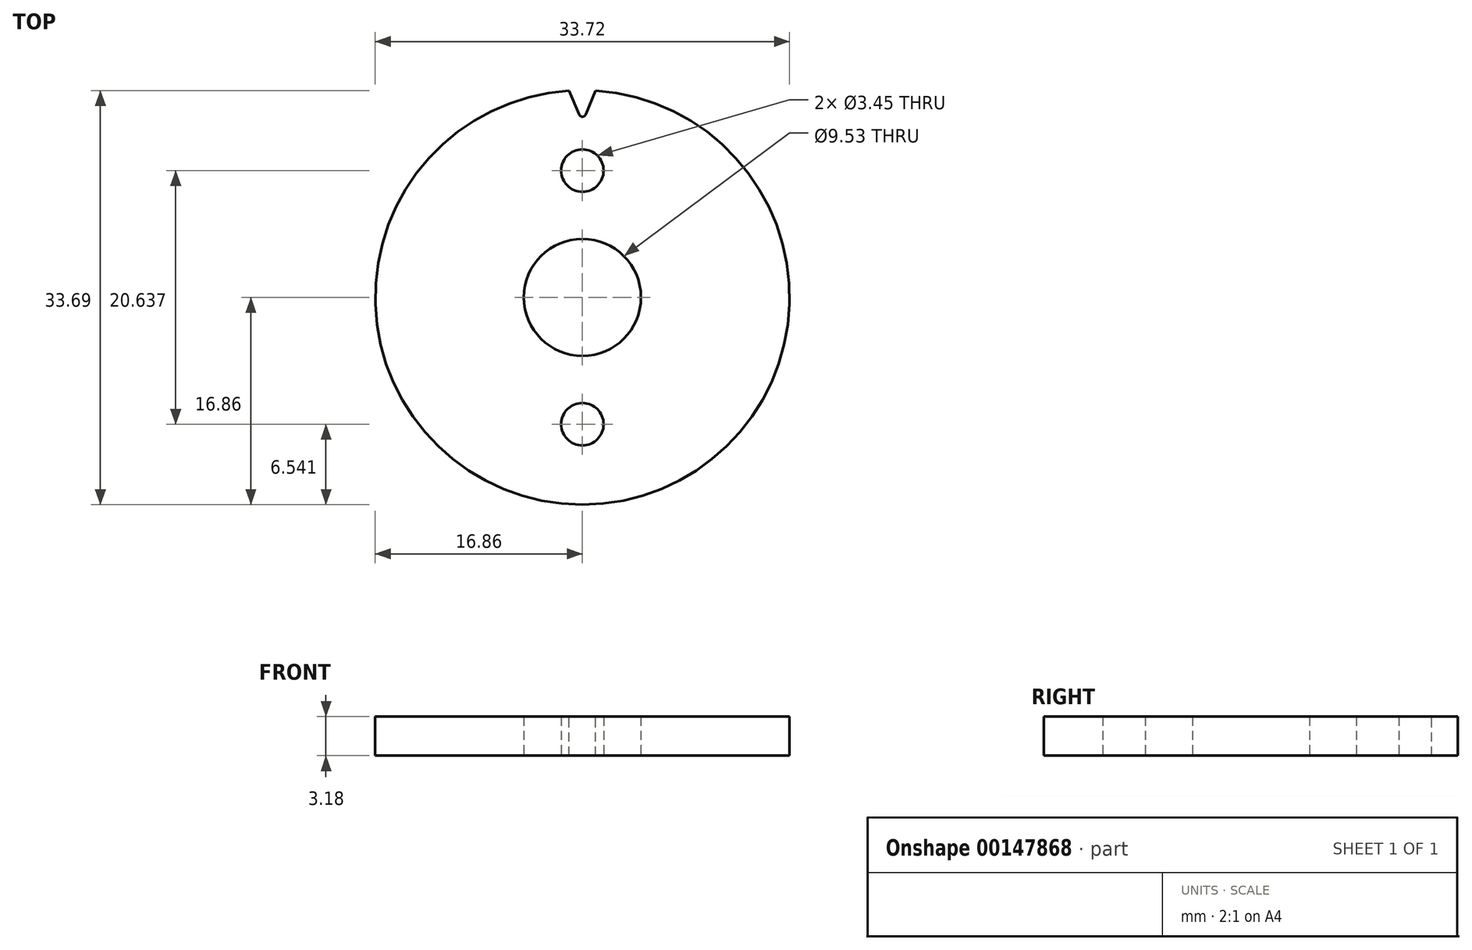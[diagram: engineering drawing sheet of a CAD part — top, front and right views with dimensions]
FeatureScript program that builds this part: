
annotation { "Feature Type Name" : "Feature", "Feature Type Description" : "" }
export const myFeature = defineFeature(function(context is Context, id is Id, definition is map)
    precondition{}
    {
        {
            var Q0;
            Q0=qCreatedBy(makeId("Top.planeOp"),FACE);
            var sketch = newSketch(context, id + "F0", { "sketchPlane" : qUnion([Q0])});
            skCircle(sketch, "E0", {"center": v(0, 0) * mm, "radius": 16.86 * mm});
            skCircle(sketch, "E1", {"center": v(0, -10.32) * mm, "radius": 5.56 * mm, "construction": true});
            skCircle(sketch, "E2", {"center": v(0, -10.32) * mm, "radius": 1.73 * mm});
            skLineSegment(sketch, "E3", {"start": v(0, 10.32) * mm, "end": v(0, -10.32) * mm, "construction": true});
            skCircle(sketch, "E4", {"center": v(0, 10.32) * mm, "radius": 1.73 * mm});
            skCircle(sketch, "E5", {"center": v(0, 0) * mm, "radius": 4.76 * mm});
            skSolve(sketch);
        }
        {
            var Q0;
            Q0=makeQuery(id+"F0.imprint","IMPRINT",FACE,{"disambiguationData":[TD([[makeQuery(id+"F0.imprint","IMPRINT",EDGE,{"derivedFrom":sQuery(id+"F0.wireOp",EDGE,"d7zeTPih-CRss-xDOh-gPdP-rmPCdwzH7cdN.left")}),1.0]])]});
            var Q1;
            Q1=makeQuery(id+"F0.imprint","IMPRINT",FACE,{"disambiguationData":[TD([[makeQuery(id+"F0.imprint","IMPRINT",EDGE,{"derivedFrom":sQuery(id+"F0.wireOp",EDGE,"E0")}),1.0]])]});
            extrude(context, id + "F1", {"entities" : qUnion([Q0, Q1]), "depth" : 3.17 * mm});
        }
        {
            var Q0;
            Q0=makeQuery(id+"F1.opExtrude","CAP_FACE",FACE,{"disambiguationData":[OSD([sQuery(id+"F0.wireOp",EDGE,"d7zeTPih-CRss-xDOh-gPdP-rmPCdwzH7cdN.left"),sQuery(id+"F0.wireOp",EDGE,"d7zeTPih-CRss-xDOh-gPdP-rmPCdwzH7cdN.right"),sQuery(id+"F0.wireOp",EDGE,"ScfBMfkV-s1yN-Ls9R-SGr5-fEyGpD6zak8e"),sQuery(id+"F0.wireOp",EDGE,"xnxmVwjl-FvSF-m7sj-be2U-u85gZZGoORGZ"),sQuery(id+"F0.wireOp",EDGE,"E0")])],"isStart":false});
            var sketch = newSketch(context, id + "F2", { "sketchPlane" : qUnion([Q0])});
            skLineSegment(sketch, "E6", {"start": v(0, 0) * mm, "end": v(0, 16.86) * mm, "construction": true});
            skLineSegment(sketch, "E7", {"start": v(0, 0) * mm, "end": v(0.72, 16.85) * mm, "construction": true});
            skArc(sketch, "E8", {"start": v(1.08, 16.83) * mm, "mid": v(0, 16.86) * mm, "end": v(-1.08, 16.83) * mm});
            skLineSegment(sketch, "E9", {"start": v(-1.08, 16.83) * mm, "end": v(-0.28, 14.88) * mm});
            skLineSegment(sketch, "E10", {"start": v(1.08, 16.83) * mm, "end": v(0.28, 14.88) * mm});
            skPoint(sketch, "E11", {"position": v(0.68, 15.85) * mm});
            skArc(sketch, "E12", {"start": v(-0.28, 14.88) * mm, "mid": v(0, 14.7) * mm, "end": v(0.28, 14.88) * mm});
            skSolve(sketch);
        }
        {
            var Q0;
            Q0=qSketchRegion(id+"F2",true);
            var Q1;
            Q1=makeQuery(id+"F1.opExtrude","CAP_FACE",FACE,{"disambiguationData":[OSD([sQuery(id+"F0.wireOp",EDGE,"d7zeTPih-CRss-xDOh-gPdP-rmPCdwzH7cdN.left"),sQuery(id+"F0.wireOp",EDGE,"d7zeTPih-CRss-xDOh-gPdP-rmPCdwzH7cdN.right"),sQuery(id+"F0.wireOp",EDGE,"ScfBMfkV-s1yN-Ls9R-SGr5-fEyGpD6zak8e"),sQuery(id+"F0.wireOp",EDGE,"xnxmVwjl-FvSF-m7sj-be2U-u85gZZGoORGZ"),sQuery(id+"F0.wireOp",EDGE,"E0")])],"isStart":true});
            extrude(context, id + "F3", {"entities" : qUnion([Q0]), "operationType" : NewBodyOperationType.REMOVE, "endBound" : BoundingType.UP_TO_SURFACE, "oppositeDirection" : true, "endBoundEntityFace" : qUnion([Q1]), "depth" : 25.4 * mm});
        }
    });
